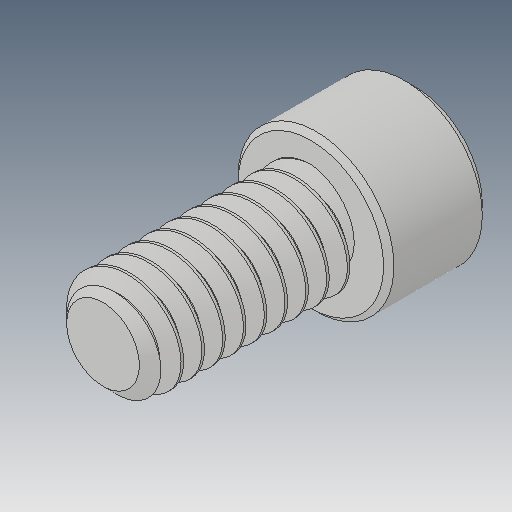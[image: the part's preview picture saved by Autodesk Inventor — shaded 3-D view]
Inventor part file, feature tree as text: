
AUTODESK INVENTOR PART (.ipt)
format: ipt  version: 2018 (Build 220112000, 112)  size: 527,360 bytes
history: native  units: in
note: dims shown in document units (in); Inventor stores cm internally (conversion verified against a paired STEP export)
features: chamfer x1
ambient origin geometry x8: Origin, YZ Plane, XZ Plane, XY Plane, X Axis, Y Axis, Z Axis, Center Point
bodies: Solid1 (feature_tree)
feature tree (1):
  chamfer  "Chamfer2"  [1 undecoded]
note: 1 required parameter value undecoded (feature->parameter linkage not recoverable at this tier; creation-order binding heuristic only, values carry confidence <= 0.55)
